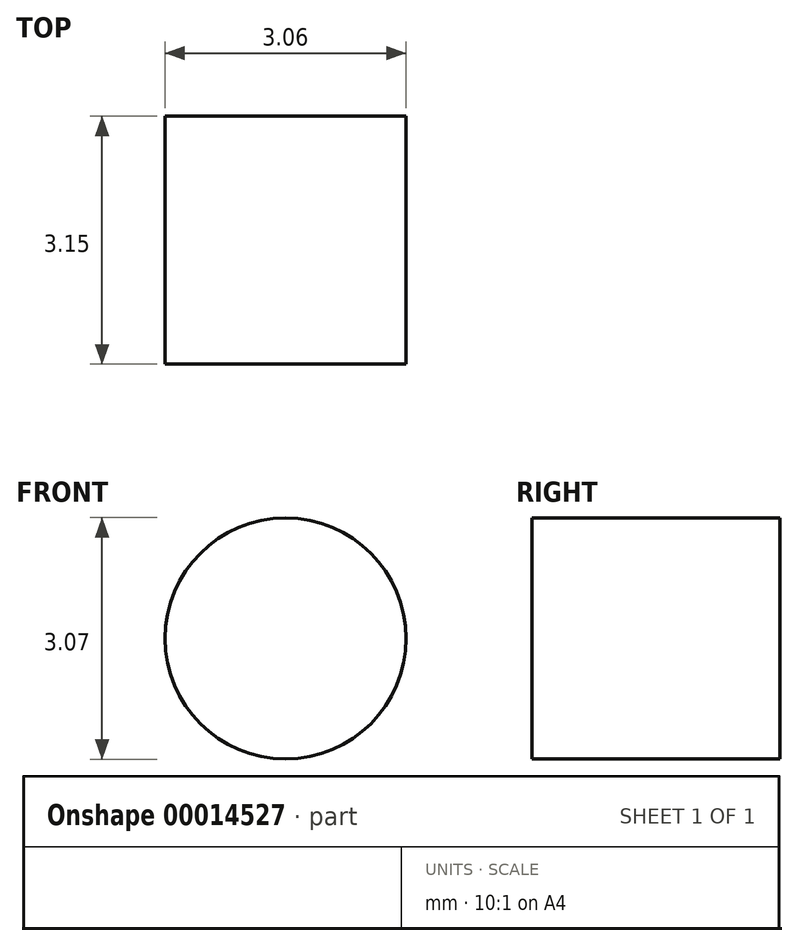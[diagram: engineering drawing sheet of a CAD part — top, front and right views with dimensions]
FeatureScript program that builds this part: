
annotation { "Feature Type Name" : "Feature", "Feature Type Description" : "" }
export const myFeature = defineFeature(function(context is Context, id is Id, definition is map)
    precondition{}
    {
        {
            var Q0;
            Q0=qCreatedBy(makeId("Front.planeOp"),FACE);
            var sketch = newSketch(context, id + "F0", { "sketchPlane" : qUnion([Q0])});
            skCircle(sketch, "E0", {"center": v(-44.07, 32.37) * mm, "radius": 1.53 * mm});
            skSolve(sketch);
        }
        {
            var Q0;
            Q0 = qSketchRegion(id + "F0", true);
            extrude(context, id + "F1", {"entities" : qUnion([Q0]), "depth" : 3.15 * mm});
        }
    });
